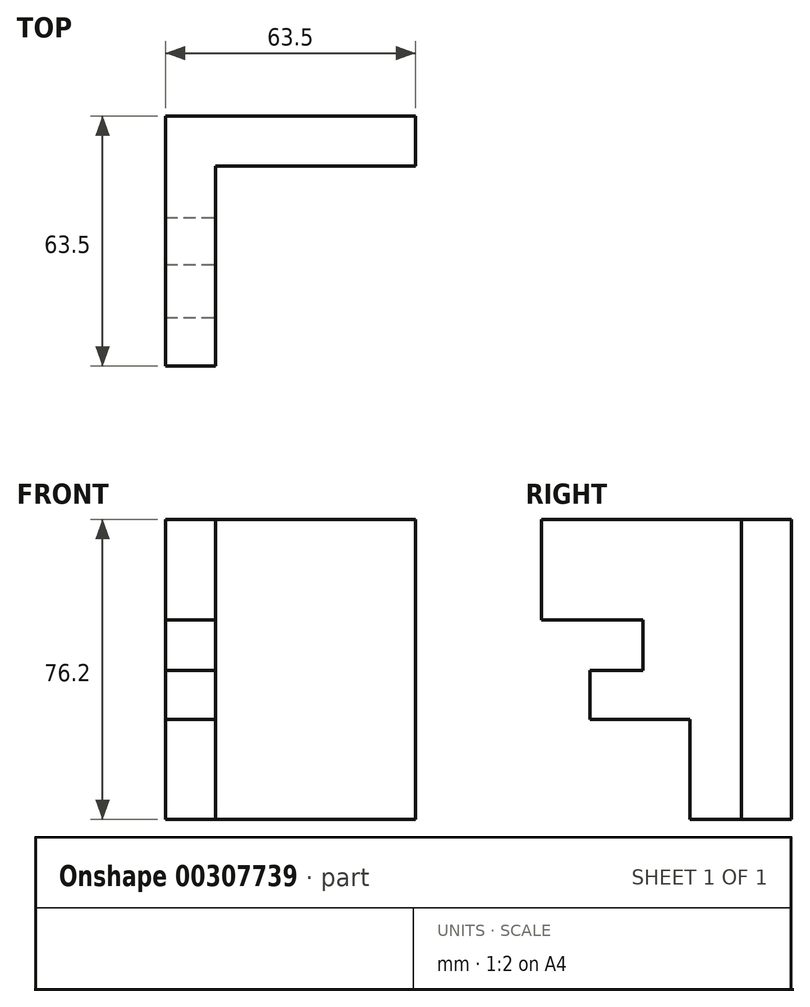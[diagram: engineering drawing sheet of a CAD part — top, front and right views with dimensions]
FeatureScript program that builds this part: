
annotation { "Feature Type Name" : "Feature", "Feature Type Description" : "" }
export const myFeature = defineFeature(function(context is Context, id is Id, definition is map)
    precondition{}
    {
        {
            var Q0;
            Q0=qCreatedBy(makeId("Top.planeOp"),FACE);
            var sketch = newSketch(context, id + "F0", { "sketchPlane" : qUnion([Q0])});
            skLineSegment(sketch, "E0", {"start": v(-43.84, -32.38) * mm, "end": v(-43.84, 31.12) * mm});
            skLineSegment(sketch, "E1", {"start": v(-43.84, 31.12) * mm, "end": v(19.66, 31.12) * mm});
            skLineSegment(sketch, "E2", {"start": v(19.66, 31.12) * mm, "end": v(19.66, 18.42) * mm});
            skLineSegment(sketch, "E3", {"start": v(-43.84, -32.38) * mm, "end": v(-31.14, -32.38) * mm});
            skLineSegment(sketch, "E4", {"start": v(-31.14, -32.38) * mm, "end": v(-31.14, 18.42) * mm});
            skLineSegment(sketch, "E5", {"start": v(-31.14, 18.42) * mm, "end": v(19.66, 18.42) * mm});
            skSolve(sketch);
        }
        {
            var Q0;
            Q0=makeQuery(id+"F0.imprint","IMPRINT",FACE,{"disambiguationData":[TD([[makeQuery(id+"F0.imprint","IMPRINT",EDGE,{"derivedFrom":sQuery(id+"F0.wireOp",EDGE,"E0")}),-1.0]])]});
            extrude(context, id + "F1", {"entities" : qUnion([Q0]), "depth" : 76.2 * mm});
        }
        {
            var Q0;
            Q0=makeQuery(id+"F1.opExtrude","SWEPT_FACE",FACE,{"disambiguationData":[OSD([sQuery(id+"F0.wireOp",EDGE,"E4")])]});
            var sketch = newSketch(context, id + "F2", { "sketchPlane" : qUnion([Q0])});
            skLineSegment(sketch, "E6", {"start": v(-32.38, 0) * mm, "end": v(-32.38, 50.68) * mm});
            skLineSegment(sketch, "E7", {"start": v(-32.38, 50.68) * mm, "end": v(-6.64, 50.68) * mm});
            skLineSegment(sketch, "E8", {"start": v(-6.64, 50.68) * mm, "end": v(-6.64, 37.86) * mm});
            skLineSegment(sketch, "E9", {"start": v(-6.64, 37.86) * mm, "end": v(-20.06, 37.86) * mm});
            skLineSegment(sketch, "E10", {"start": v(-20.06, 37.86) * mm, "end": v(-20.06, 25.45) * mm});
            skLineSegment(sketch, "E11", {"start": v(-20.06, 25.45) * mm, "end": v(5.37, 25.45) * mm});
            skLineSegment(sketch, "E12", {"start": v(5.37, 25.45) * mm, "end": v(5.37, 0) * mm});
            skLineSegment(sketch, "E13", {"start": v(5.37, 0) * mm, "end": v(-32.38, 0) * mm});
            skSolve(sketch);
        }
        {
            var Q0;
            Q0=makeQuery(id+"F2.imprint","IMPRINT",FACE,{"disambiguationData":[TD([[makeQuery(id+"F2.imprint","IMPRINT",EDGE,{"derivedFrom":sQuery(id+"F2.wireOp",EDGE,"E6")}),1.0]])]});
            extrude(context, id + "F3", {"entities" : qUnion([Q0]), "operationType" : NewBodyOperationType.REMOVE, "oppositeDirection" : true, "depth" : 25.4 * mm});
        }
    });
